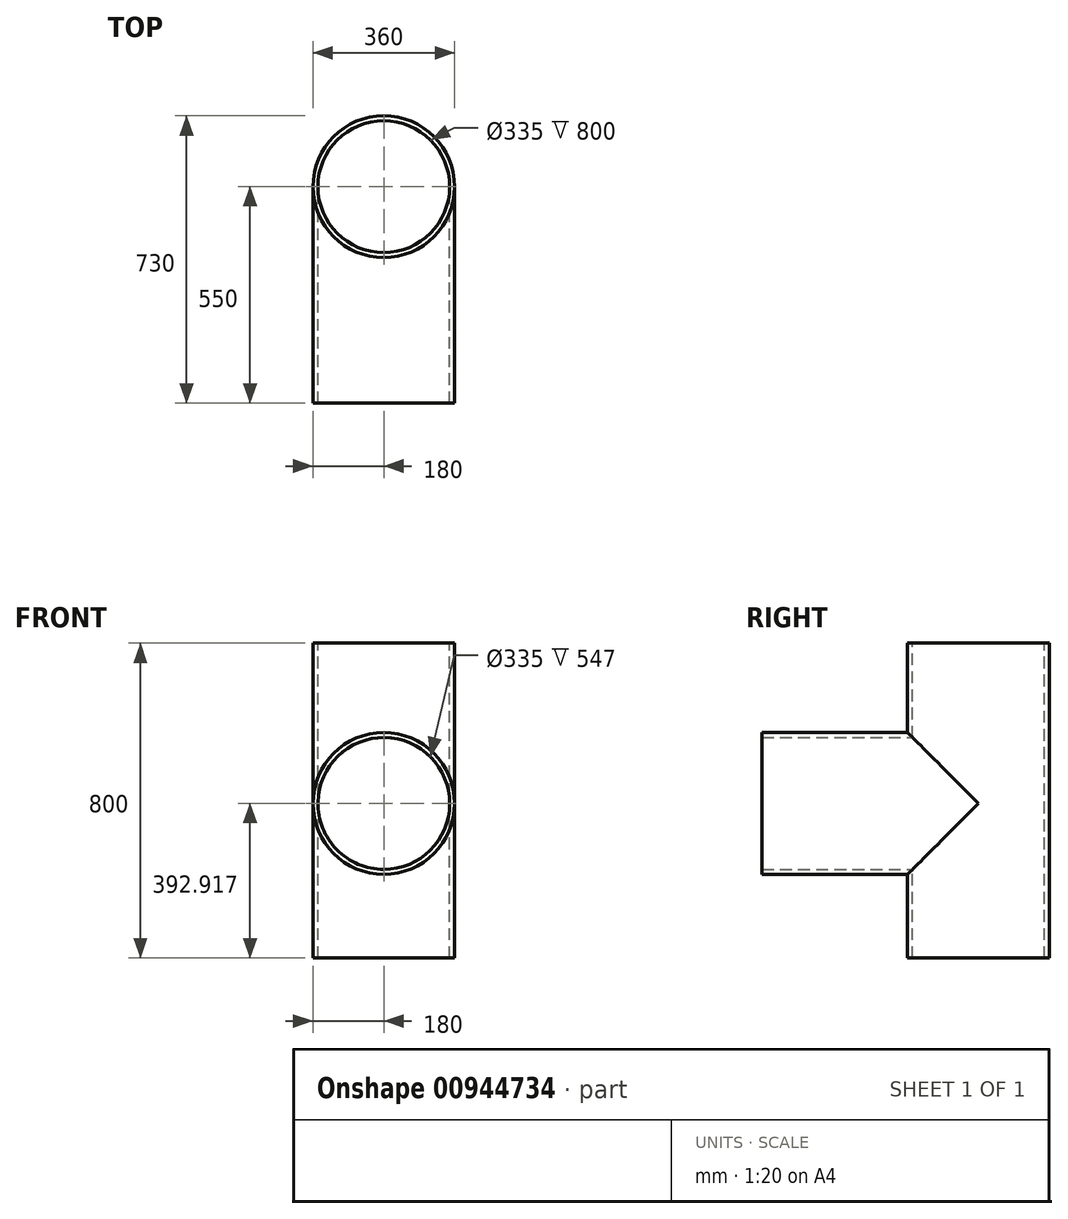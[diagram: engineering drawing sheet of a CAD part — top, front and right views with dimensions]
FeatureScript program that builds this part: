
annotation { "Feature Type Name" : "Feature", "Feature Type Description" : "" }
export const myFeature = defineFeature(function(context is Context, id is Id, definition is map)
    precondition{}
    {
        {
            var Q0;
            Q0=qCreatedBy(makeId("Top.planeOp"),FACE);
            var sketch = newSketch(context, id + "F0", { "sketchPlane" : qUnion([Q0])});
            skCircle(sketch, "E0", {"center": v(0, 0) * mm, "radius": 180 * mm});
            skCircle(sketch, "E1", {"center": v(0, 0) * mm, "radius": 167.5 * mm});
            skSolve(sketch);
        }
        {
            var Q0;
            Q0=makeQuery(id+"F0.imprint","IMPRINT",FACE,{"disambiguationData":[TD([[makeQuery(id+"F0.imprint","IMPRINT",EDGE,{"derivedFrom":sQuery(id+"F0.wireOp",EDGE,"E0")}),1.0]])]});
            extrude(context, id + "F1", {"entities" : qUnion([Q0]), "oppositeDirection" : true, "depth" : 800 * mm, "offsetDistance" : 25 * mm});
        }
        {
            var Q0;
            Q0=qCreatedBy(makeId("Front.planeOp"),FACE);
            var sketch = newSketch(context, id + "F2", { "sketchPlane" : qUnion([Q0])});
            skLineSegment(sketch, "E2", {"start": v(0, 0) * mm, "end": v(0, -814.17) * mm});
            skCircle(sketch, "E3", {"center": v(0, -407.08) * mm, "radius": 180 * mm});
            skCircle(sketch, "E4", {"center": v(0, -407.08) * mm, "radius": 167.5 * mm});
            skSolve(sketch);
        }
        {
            var Q0;
            Q0 = qSketchRegion(id + "F2", true);
            extrude(context, id + "F3", {"entities" : qUnion([Q0]), "operationType" : NewBodyOperationType.ADD, "depth" : 550 * mm, "offsetDistance" : 25 * mm});
        }
        {
            var Q0;
            Q0=qCreatedBy(makeId("Top.planeOp"),FACE);
            var sketch = newSketch(context, id + "F4", { "sketchPlane" : qUnion([Q0])});
            skCircle(sketch, "E5", {"center": v(0, 0) * mm, "radius": 167.5 * mm});
            skSolve(sketch);
        }
        {
            var Q0;
            Q0 = qSketchRegion(id + "F4", true);
            extrude(context, id + "F5", {"entities" : qUnion([Q0]), "operationType" : NewBodyOperationType.REMOVE, "endBound" : BoundingType.THROUGH_ALL, "oppositeDirection" : true, "depth" : 25 * mm, "offsetDistance" : 25 * mm});
        }
        {
            var Q0;
            Q0=makeQuery(id+"F3.opExtrude","CAP_FACE",FACE,{"disambiguationData":[OSD([sQuery(id+"F2.wireOp",EDGE,"E3"),sQuery(id+"F2.wireOp",EDGE,"E4")])],"isStart":false});
            var sketch = newSketch(context, id + "F6", { "sketchPlane" : qUnion([Q0])});
            skCircle(sketch, "E6", {"center": v(0, -407.08) * mm, "radius": 167.5 * mm});
            skSolve(sketch);
        }
        {
            var Q0;
            Q0 = qSketchRegion(id + "F6", true);
            extrude(context, id + "F7", {"entities" : qUnion([Q0]), "operationType" : NewBodyOperationType.REMOVE, "oppositeDirection" : true, "depth" : 547 * mm, "offsetDistance" : 25 * mm});
        }
    });
